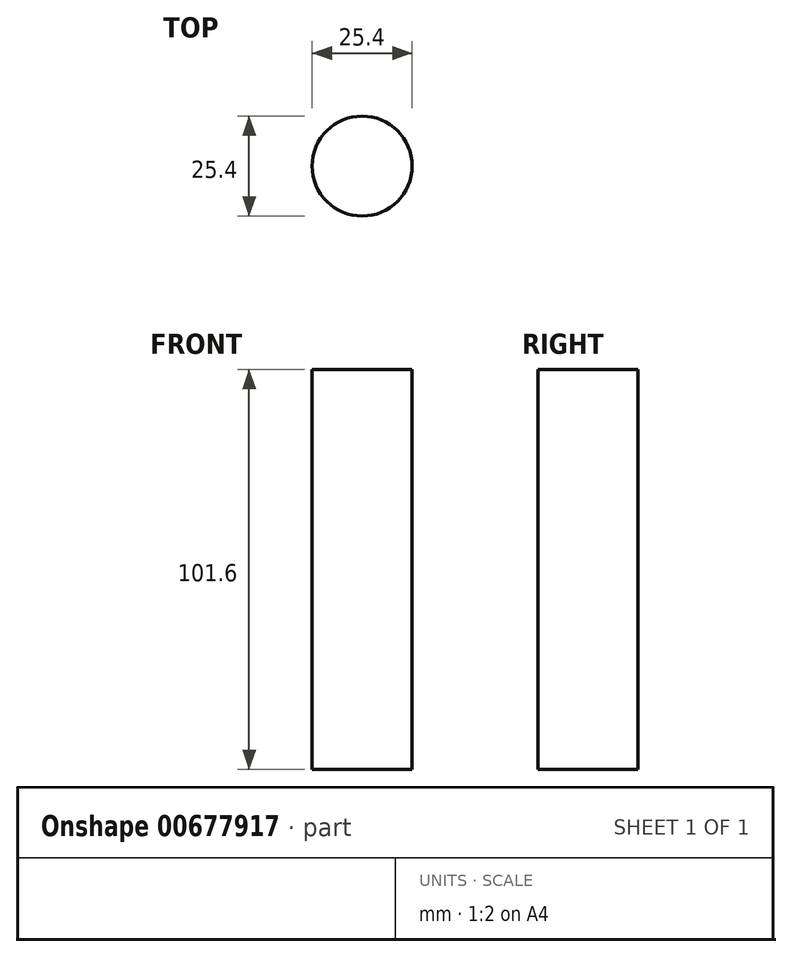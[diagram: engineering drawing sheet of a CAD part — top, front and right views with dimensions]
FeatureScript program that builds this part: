
annotation { "Feature Type Name" : "Feature", "Feature Type Description" : "" }
export const myFeature = defineFeature(function(context is Context, id is Id, definition is map)
    precondition{}
    {
        {
            var Q0;
            Q0=qCreatedBy(makeId("Top.planeOp"),FACE);
            var sketch = newSketch(context, id + "F0", { "sketchPlane" : qUnion([Q0])});
            skPoint(sketch, "E0", {"position": v(32, 31) * mm});
            skCircle(sketch, "E1", {"center": v(32, 31) * mm, "radius": 12.7 * mm});
            skSolve(sketch);
        }
        {
            var Q0;
            Q0 = qSketchRegion(id + "F0", true);
            extrude(context, id + "F1", {"entities" : qUnion([Q0]), "depth" : 101.6 * mm, "offsetDistance" : 25.4 * mm});
        }
    });
